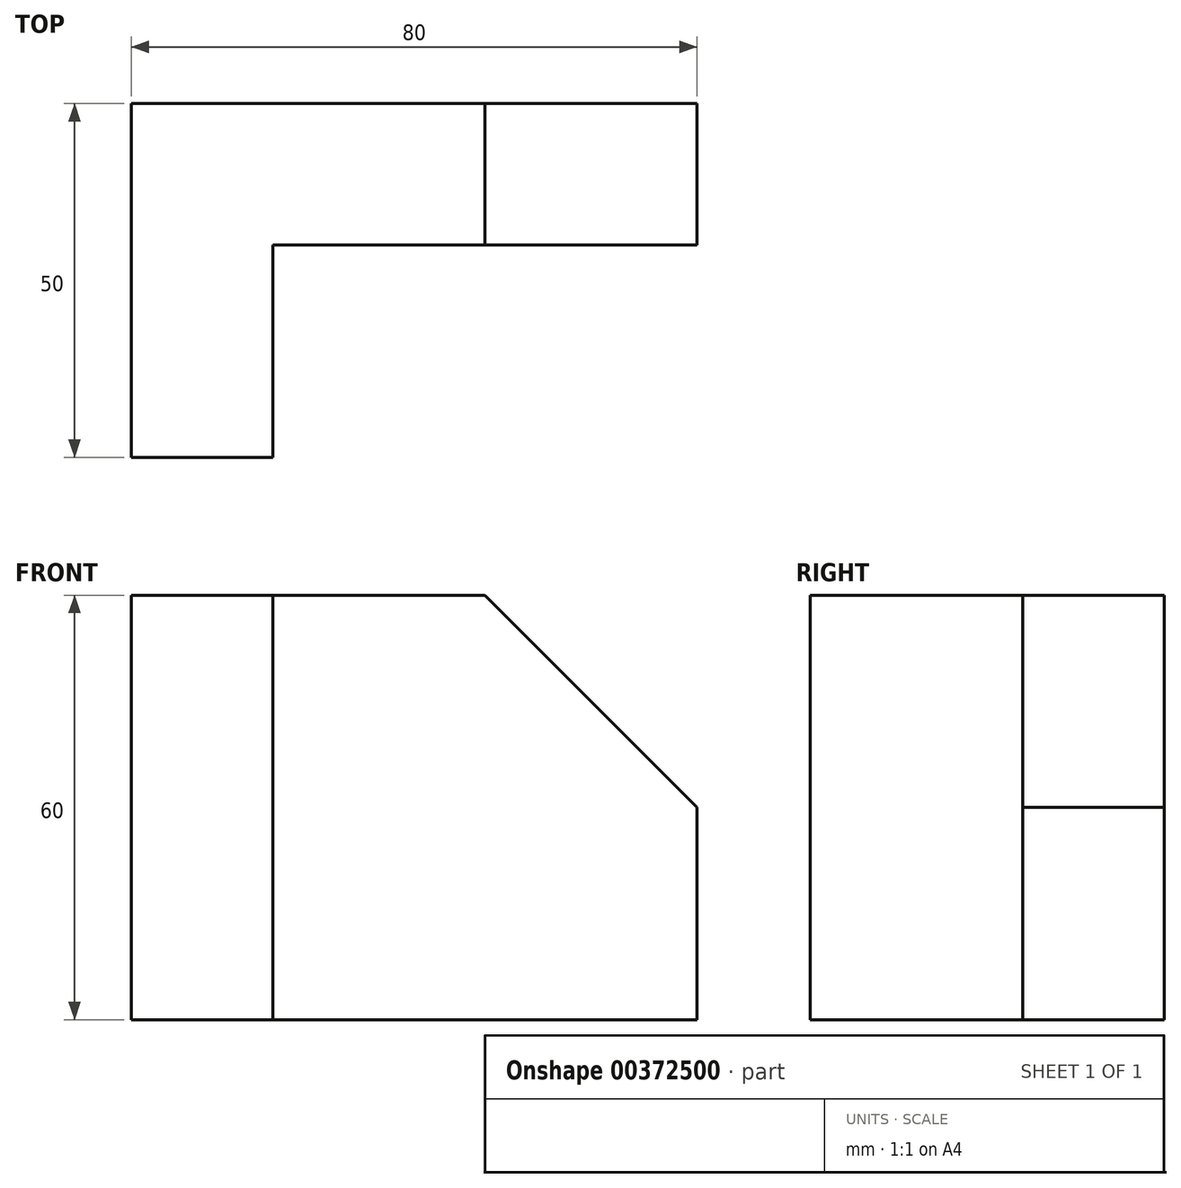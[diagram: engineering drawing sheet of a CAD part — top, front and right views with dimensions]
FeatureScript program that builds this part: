
annotation { "Feature Type Name" : "Feature", "Feature Type Description" : "" }
export const myFeature = defineFeature(function(context is Context, id is Id, definition is map)
    precondition{}
    {
        {
            var Q0;
            Q0=qCreatedBy(makeId("Front.planeOp"),FACE);
            var sketch = newSketch(context, id + "F0", { "sketchPlane" : qUnion([Q0])});
            skLineSegment(sketch, "E0.bottom", {"start": v(40, -30) * mm, "end": v(-40, -30) * mm});
            skLineSegment(sketch, "E0.top", {"start": v(40, 30) * mm, "end": v(-40, 30) * mm});
            skLineSegment(sketch, "E0.left", {"start": v(40, -30) * mm, "end": v(40, 30) * mm});
            skLineSegment(sketch, "E0.right", {"start": v(-40, -30) * mm, "end": v(-40, 30) * mm});
            skPoint(sketch, "E0.middle", {"position": v(0, 0) * mm});
            skSolve(sketch);
        }
        {
            var Q0;
            Q0=makeQuery(id+"F0.imprint","IMPRINT",FACE,{"disambiguationData":[TD([[makeQuery(id+"F0.imprint","IMPRINT",EDGE,{"derivedFrom":sQuery(id+"F0.wireOp",EDGE,"E0.bottom")}),-1.0]])]});
            extrude(context, id + "F1", {"entities" : qUnion([Q0]), "depth" : 20 * mm});
        }
        {
            var Q0;
            Q0=makeQuery(id+"F1.opExtrude","CAP_FACE",FACE,{"disambiguationData":[OSD([sQuery(id+"F0.wireOp",EDGE,"E0.bottom"),sQuery(id+"F0.wireOp",EDGE,"E0.top"),sQuery(id+"F0.wireOp",EDGE,"E0.left"),sQuery(id+"F0.wireOp",EDGE,"E0.right")])],"isStart":false});
            var sketch = newSketch(context, id + "F2", { "sketchPlane" : qUnion([Q0])});
            skLineSegment(sketch, "E1", {"start": v(-20, 30) * mm, "end": v(-20, -30) * mm});
            skSolve(sketch);
        }
        {
            var Q0;
            {var subQ0=sQuery(id+"F2.wireOp",EDGE,"E1");Q0=makeQuery(id+"F2.imprint","IMPRINT",FACE,{"disambiguationData":[TD([[makeQuery(id+"F2.imprint","IMPRINT",EDGE,{"derivedFrom":subQ0}),-1.0]])]});}
            extrude(context, id + "F3", {"entities" : qUnion([Q0]), "operationType" : NewBodyOperationType.ADD, "depth" : 30 * mm});
        }
        {
            var Q0;
            Q0=makeQuery(id+"F1.opExtrude","CAP_FACE",FACE,{"disambiguationData":[OSD([sQuery(id+"F0.wireOp",EDGE,"E0.bottom"),sQuery(id+"F0.wireOp",EDGE,"E0.top"),sQuery(id+"F0.wireOp",EDGE,"E0.left"),sQuery(id+"F0.wireOp",EDGE,"E0.right")])],"isStart":false});
            var sketch = newSketch(context, id + "F4", { "sketchPlane" : qUnion([Q0])});
            skLineSegment(sketch, "E2", {"start": v(10, 30) * mm, "end": v(10, 0) * mm, "construction": true});
            skLineSegment(sketch, "E3", {"start": v(10, 0) * mm, "end": v(40, 0) * mm, "construction": true});
            skLineSegment(sketch, "E4", {"start": v(10, 30) * mm, "end": v(40, 0) * mm});
            skSolve(sketch);
        }
        {
            var Q0;
            Q0 = qSketchRegion(id + "F4", true);
            var Q1;
            {var subQ0=sQuery(id+"F4.wireOp",EDGE,"E4");Q1=makeQuery(id+"F4.imprint","IMPRINT",FACE,{"disambiguationData":[TD([[makeQuery(id+"F4.imprint","IMPRINT",EDGE,{"derivedFrom":subQ0}),1.0]])]});}
            extrude(context, id + "F5", {"entities" : qUnion([Q0, Q1]), "operationType" : NewBodyOperationType.REMOVE, "endBound" : BoundingType.THROUGH_ALL, "oppositeDirection" : true, "depth" : 25 * mm});
        }
    });
